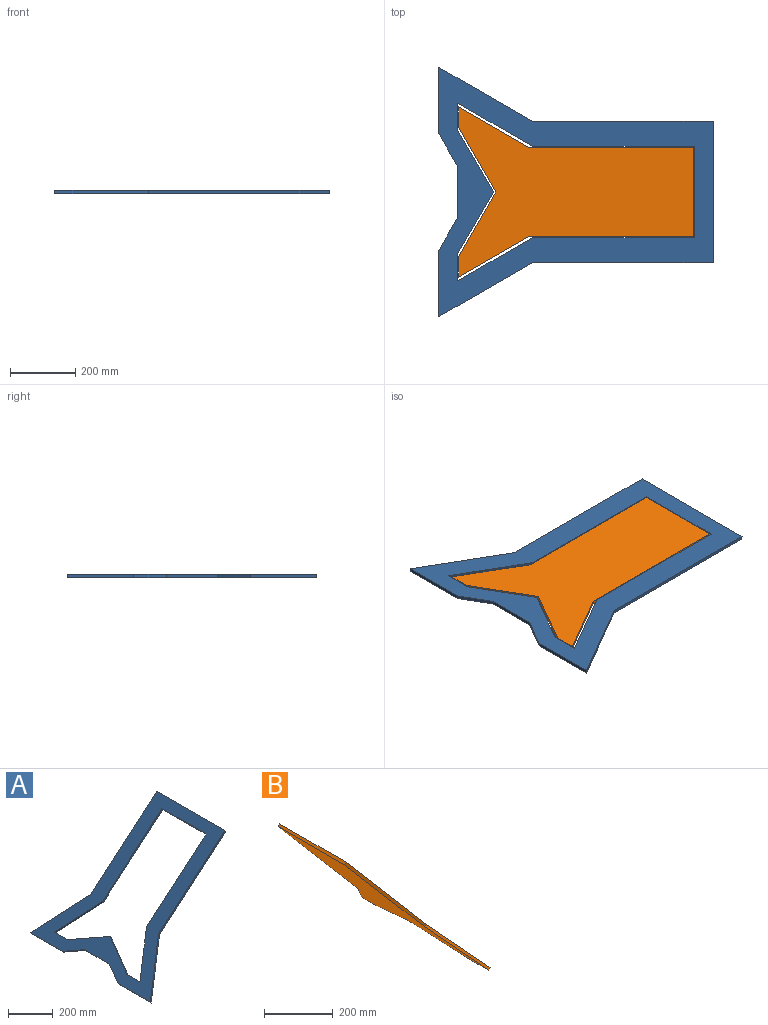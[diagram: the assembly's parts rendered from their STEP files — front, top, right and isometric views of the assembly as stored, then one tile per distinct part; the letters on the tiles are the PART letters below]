
ASSEMBLY  parts=2 mates=1
PART A: 21 faces, bbox 644.9x762x549.8 mm
  f0: plane 203.2x7.26mm, normal (-0.76,0,-0.65), area 1935.5mm2, adj f2,f3,f7,f19
  f1: plane 431.8x7.26mm, normal (0.76,0,0.65), area 4112.9mm2, adj f2,f3,f5,f20
  f2: plane 762x638.69mm, normal (-0.65,0,0.76), area 182650.4mm2, adj f0,f1,f4,f5,f6,f7,f8,f9
  f3: plane 762x638.69mm, normal (0.65,0,-0.76), area 182650.4mm2, adj f0,f1,f4,f5,f6,f7,f8,f9
  f4: plane 203.2x7.26mm, normal (-0.76,0,-0.65), area 1935.5mm2, adj f2,f3,f6,f9
  f5: plane 426.92x364.68mm, normal (0,1,0), area 5258.5mm2, adj f1,f2,f3,f6
  f6: plane 224.11x192.4mm, normal (0.38,0.87,0.32), area 3145.2mm2, adj f2,f3,f4,f5
  f7: plane 98.99x49.72mm, normal (-0.66,0.5,-0.56), area 1088.7mm2, adj f0,f2,f3,f8
  f8: plane 157.63x7.26mm, normal (-0.76,0,-0.65), area 1501.4mm2, adj f2,f3,f7,f9
  f9: plane 98.99x49.72mm, normal (-0.66,-0.5,-0.56), area 1088.7mm2, adj f2,f3,f4,f8
  f10: plane 189.25x89.44mm, normal (0.66,-0.5,0.56), area 2081.5mm2, adj f2,f3,f11,f18
  f11: plane 82.55x7.26mm, normal (0.76,0,0.65), area 786.3mm2, adj f2,f3,f10,f12
  f12: plane 180.55x155.4mm, normal (-0.38,0.87,-0.32), area 2516.6mm2, adj f2,f3,f11,f13
  f13: plane 383.36x327.68mm, normal (0,1,0), area 4714.1mm2, adj f2,f3,f12,f14
  f14: plane 279.4x7.26mm, normal (-0.76,0,-0.65), area 2661.3mm2, adj f2,f3,f13,f15
  f15: plane 383.36x327.68mm, normal (0,-1,0), area 4714.1mm2, adj f2,f3,f14,f16
  f16: plane 180.55x155.4mm, normal (-0.38,-0.87,-0.32), area 2516.6mm2, adj f2,f3,f15,f17
  f17: plane 82.55x7.26mm, normal (0.76,0,0.65), area 786.3mm2, adj f2,f3,f16,f18
  f18: plane 189.25x89.44mm, normal (0.66,0.5,0.56), area 2081.5mm2, adj f2,f3,f10,f17
  f19: plane 224.11x192.4mm, normal (0.38,-0.87,0.32), area 3145.2mm2, adj f0,f2,f3,f20
  f20: plane 426.92x364.68mm, normal (0,-1,0), area 5258.5mm2, adj f1,f2,f3,f19
PART B: 11 faces, bbox 474.7x520.7x552.3 mm
  f0: plane 546.12x520.7mm, normal (0.76,0,0.65), area 200464mm2, adj f1,f2,f3,f5,f6,f7,f8,f9
  f1: plane 273.05x7.24mm, normal (-0.65,0,0.76), area 2600.8mm2, adj f0,f4,f5,f9
  f2: plane 63.5x7.24mm, normal (0.65,0,-0.76), area 604.8mm2, adj f0,f4,f8,f10
  f3: plane 63.5x7.24mm, normal (0.65,0,-0.76), area 604.8mm2, adj f0,f4,f6,f7
  f4: plane 546.12x520.7mm, normal (-0.76,0,-0.65), area 200464mm2, adj f1,f2,f3,f5,f6,f7,f8,f9
  f5: plane 389.38x335.2mm, normal (0,-1,0), area 4804.1mm2, adj f0,f1,f4,f6
  f6: plane 169.13x146.7mm, normal (-0.33,-0.87,0.38), area 2358.9mm2, adj f0,f3,f4,f5
  f7: plane 196.85x92.54mm, normal (0.56,0.5,-0.66), area 2165.1mm2, adj f0,f3,f4,f8
  f8: plane 196.85x92.54mm, normal (0.56,-0.5,-0.66), area 2165.1mm2, adj f0,f2,f4,f7
  f9: plane 389.38x335.2mm, normal (0,1,0), area 4804.1mm2, adj f0,f1,f4,f10
  f10: plane 169.13x146.7mm, normal (-0.33,0.87,0.38), area 2358.9mm2, adj f0,f2,f4,f9
PLACE A rot(axis=(0,1,0),40.3deg) t=(-272.32,0,15.87)mm
PLACE B rot(axis=(0,1,0),130.6deg) t=(-285.14,0,-25.4)mm
MATE fastened B.f4 <-> A.f2  axis (0,0,1) through (-2.03,0,0)mm
